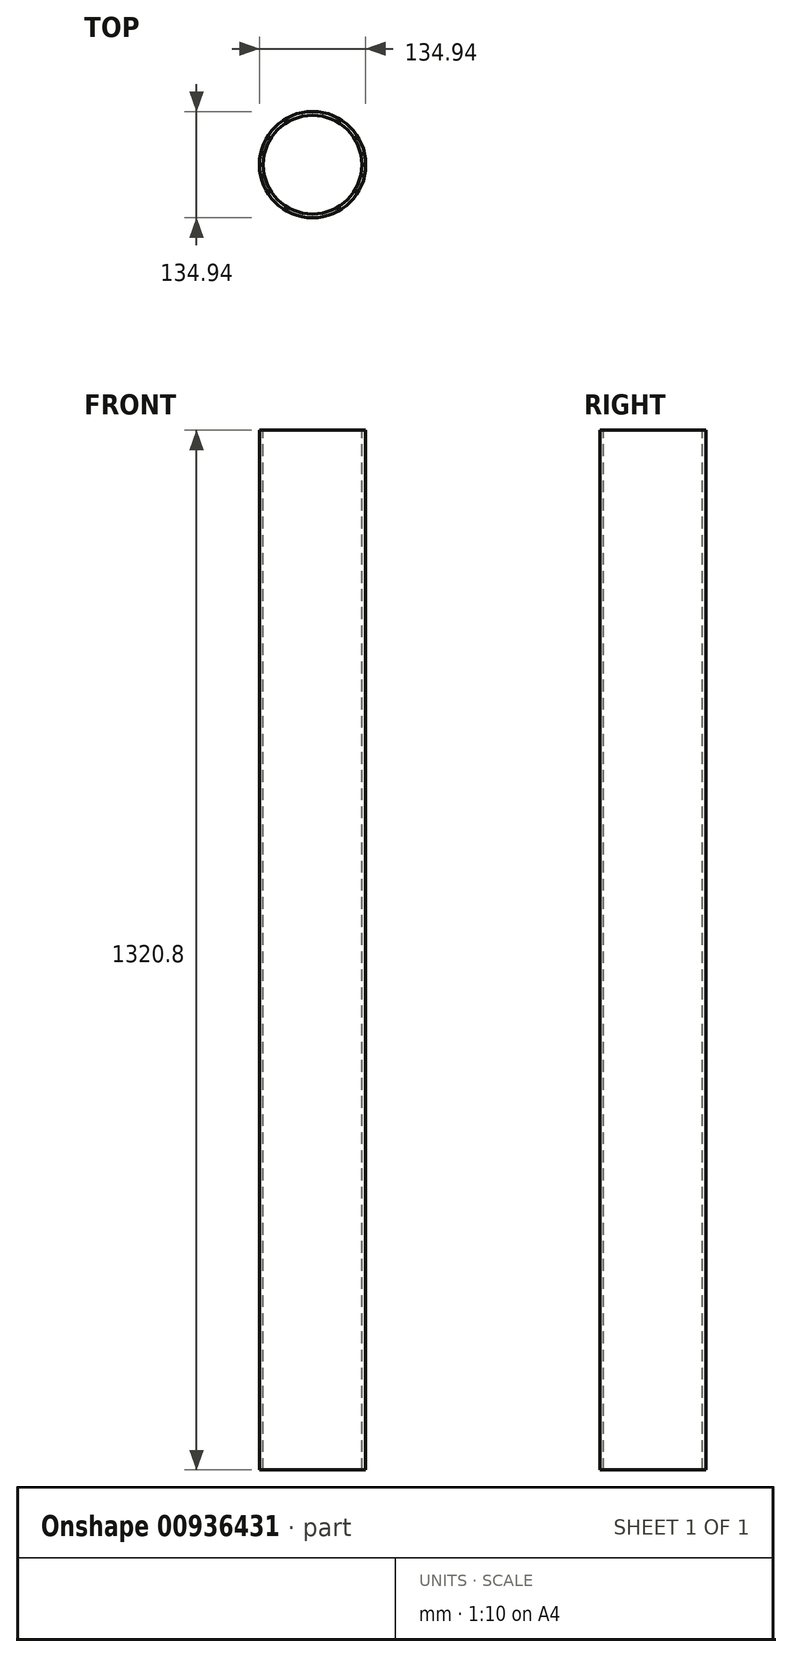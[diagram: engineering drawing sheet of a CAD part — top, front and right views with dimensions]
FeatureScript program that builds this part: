
annotation { "Feature Type Name" : "Feature", "Feature Type Description" : "" }
export const myFeature = defineFeature(function(context is Context, id is Id, definition is map)
    precondition{}
    {
        {
            var Q0;
            Q0=qCreatedBy(makeId("Top.planeOp"),FACE);
            var sketch = newSketch(context, id + "F0", { "sketchPlane" : qUnion([Q0])});
            skCircle(sketch, "E0", {"center": v(0, 0) * mm, "radius": 67.47 * mm});
            skSolve(sketch);
        }
        {
            var Q0;
            Q0=qCreatedBy(makeId("Top.planeOp"),FACE);
            var sketch = newSketch(context, id + "F1", { "sketchPlane" : qUnion([Q0])});
            skCircle(sketch, "E1", {"center": v(0, 0) * mm, "radius": 62.74 * mm});
            skSolve(sketch);
        }
        {
            var Q0;
            Q0=sQuery(id+"F0.wireOp",EDGE,"E0");
            var Q1;
            Q1=sQuery(id+"F1.wireOp",EDGE,"E1");
            extrude(context, id + "F2", {"bodyType" : ToolBodyType.SURFACE, "surfaceEntities" : qUnion([Q0, Q1]), "depth" : 1320.8 * mm, "offsetDistance" : 25.4 * mm});
        }
    });
